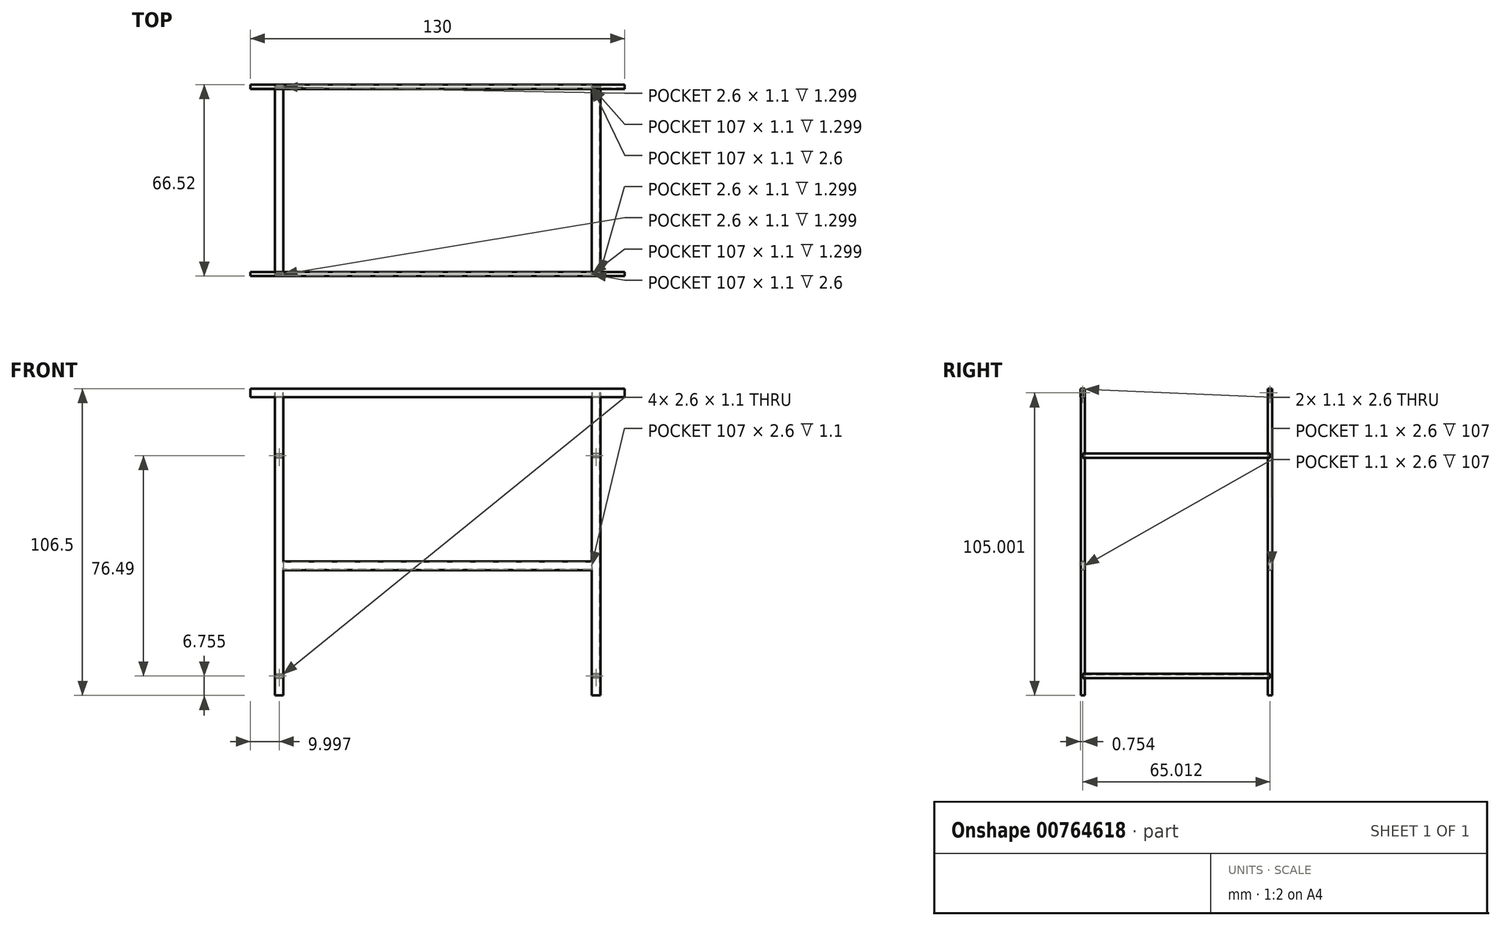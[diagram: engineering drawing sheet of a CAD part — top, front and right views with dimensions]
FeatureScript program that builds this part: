
annotation { "Feature Type Name" : "Feature", "Feature Type Description" : "" }
export const myFeature = defineFeature(function(context is Context, id is Id, definition is map)
    precondition{}
    {
        {
            var Q0;
            Q0=qCreatedBy(makeId("Top.planeOp"),FACE);
            cPlane(context, id + "F0", {"entities" : qUnion([Q0]), "cplaneType" : CPlaneType.OFFSET, "offset" : 60 * mm, "width" : 150 * mm, "height" : 150 * mm});
        }
        {
            var Q0;
            Q0=qCreatedBy(id+"F0.planeOp",FACE);
            var sketch = newSketch(context, id + "F1", { "sketchPlane" : qUnion([Q0])});
            skLineSegment(sketch, "E0", {"start": v(0, 0) * mm, "end": v(-65, 0) * mm, "construction": true});
            skLineSegment(sketch, "E1", {"start": v(-65, 0) * mm, "end": v(-65, 32.5) * mm, "construction": true});
            skSolve(sketch);
        }
        {
            var Q0;
            Q0=qCreatedBy(makeId("Right.planeOp"),FACE);
            cPlane(context, id + "F2", {"entities" : qUnion([Q0]), "cplaneType" : CPlaneType.OFFSET, "offset" : 65 * mm, "oppositeDirection" : true, "width" : 150 * mm, "height" : 150 * mm});
        }
        {
            var Q0;
            Q0=qCreatedBy(id+"F2.planeOp",FACE);
            var sketch = newSketch(context, id + "F3", { "sketchPlane" : qUnion([Q0])});
            skLineSegment(sketch, "E2.bottom", {"start": v(33.26, 61.5) * mm, "end": v(31.76, 61.5) * mm});
            skLineSegment(sketch, "E2.top", {"start": v(33.26, 58.5) * mm, "end": v(31.76, 58.5) * mm});
            skLineSegment(sketch, "E2.left", {"start": v(33.26, 61.5) * mm, "end": v(33.26, 58.5) * mm});
            skLineSegment(sketch, "E2.right", {"start": v(31.76, 61.5) * mm, "end": v(31.76, 58.5) * mm});
            skPoint(sketch, "E2.middle", {"position": v(32.5, 60) * mm});
            skLineSegment(sketch, "E3.bottom", {"start": v(33.06, 61.3) * mm, "end": v(31.96, 61.3) * mm});
            skLineSegment(sketch, "E3.top", {"start": v(33.06, 58.7) * mm, "end": v(31.96, 58.7) * mm});
            skLineSegment(sketch, "E3.left", {"start": v(33.06, 61.3) * mm, "end": v(33.06, 58.7) * mm});
            skLineSegment(sketch, "E3.right", {"start": v(31.96, 61.3) * mm, "end": v(31.96, 58.7) * mm});
            skSolve(sketch);
        }
        {
            var Q0;
            Q0=makeQuery(id+"F3.imprint","IMPRINT",FACE,{"disambiguationData":[TD([[makeQuery(id+"F3.imprint","IMPRINT",EDGE,{"derivedFrom":sQuery(id+"F3.wireOp",EDGE,"E2.bottom")}),1.0]])]});
            extrude(context, id + "F4", {"entities" : qUnion([Q0]), "depth" : 130 * mm, "offsetDistance" : 25 * mm});
        }
        {
            var Q0;
            Q0=makeQuery(id+"F4.opExtrude","SWEPT_BODY",BODY,{"disambiguationData":[OSD([sQuery(id+"F3.wireOp",EDGE,"E2.bottom"),sQuery(id+"F3.wireOp",EDGE,"E2.top"),sQuery(id+"F3.wireOp",EDGE,"E2.left"),sQuery(id+"F3.wireOp",EDGE,"E2.right"),sQuery(id+"F3.wireOp",EDGE,"E3.bottom"),sQuery(id+"F3.wireOp",EDGE,"E3.top"),sQuery(id+"F3.wireOp",EDGE,"E3.left"),sQuery(id+"F3.wireOp",EDGE,"E3.right")])]});
            var Q1;
            Q1=qCreatedBy(makeId("Front.planeOp"),FACE);
            mirror(context, id + "F5", {"entities" : qUnion([Q0]), "mirrorPlane" : qUnion([Q1])});
        }
        {
            var Q0;
            Q0=qCreatedBy(id+"F0.planeOp",FACE);
            var sketch = newSketch(context, id + "F6", { "sketchPlane" : qUnion([Q0])});
            skLineSegment(sketch, "E4", {"start": v(0, -49.29) * mm, "end": v(0, 13.23) * mm, "construction": true});
            skLineSegment(sketch, "E5", {"start": v(0, -32.5) * mm, "end": v(-55, -32.5) * mm, "construction": true});
            skLineSegment(sketch, "E6.bottom", {"start": v(-53.5, -33.25) * mm, "end": v(-56.5, -33.25) * mm});
            skLineSegment(sketch, "E6.top", {"start": v(-53.5, -31.75) * mm, "end": v(-56.5, -31.75) * mm});
            skLineSegment(sketch, "E6.left", {"start": v(-53.5, -33.25) * mm, "end": v(-53.5, -31.75) * mm});
            skLineSegment(sketch, "E6.right", {"start": v(-56.5, -33.25) * mm, "end": v(-56.5, -31.75) * mm});
            skPoint(sketch, "E6.middle", {"position": v(-55, -32.5) * mm});
            skLineSegment(sketch, "E7.bottom", {"start": v(-53.7, -33.05) * mm, "end": v(-56.3, -33.05) * mm});
            skLineSegment(sketch, "E7.top", {"start": v(-53.7, -31.95) * mm, "end": v(-56.3, -31.95) * mm});
            skLineSegment(sketch, "E7.left", {"start": v(-53.7, -33.05) * mm, "end": v(-53.7, -31.95) * mm});
            skLineSegment(sketch, "E7.right", {"start": v(-56.3, -33.05) * mm, "end": v(-56.3, -31.95) * mm});
            skSolve(sketch);
        }
        {
            var Q0;
            Q0=qSketchRegion(id+"F6",true);
            extrude(context, id + "F7", {"entities" : qUnion([Q0]), "oppositeDirection" : true, "depth" : 105 * mm, "offsetDistance" : 25 * mm});
        }
        {
            var Q0;
            Q0=makeQuery(id+"F7.opExtrude","SWEPT_BODY",BODY,{"disambiguationData":[OSD([sQuery(id+"F6.wireOp",EDGE,"E6.bottom"),sQuery(id+"F6.wireOp",EDGE,"E6.top"),sQuery(id+"F6.wireOp",EDGE,"E6.left"),sQuery(id+"F6.wireOp",EDGE,"E6.right"),sQuery(id+"F6.wireOp",EDGE,"E7.bottom"),sQuery(id+"F6.wireOp",EDGE,"E7.top"),sQuery(id+"F6.wireOp",EDGE,"E7.left"),sQuery(id+"F6.wireOp",EDGE,"E7.right")])]});
            var Q1;
            Q1=qCreatedBy(makeId("Right.planeOp"),FACE);
            mirror(context, id + "F8", {"operationType" : NewBodyOperationType.ADD, "entities" : qUnion([Q0]), "mirrorPlane" : qUnion([Q1])});
        }
        {
            var Q0;
            Q0=makeQuery(id+"F5.opPattern","COPY",BODY,{"derivedFrom":makeQuery(id+"F4.opExtrude","SWEPT_BODY",BODY,{"disambiguationData":[OSD([sQuery(id+"F3.wireOp",EDGE,"E2.bottom"),sQuery(id+"F3.wireOp",EDGE,"E2.top"),sQuery(id+"F3.wireOp",EDGE,"E2.left"),sQuery(id+"F3.wireOp",EDGE,"E2.right"),sQuery(id+"F3.wireOp",EDGE,"E3.bottom"),sQuery(id+"F3.wireOp",EDGE,"E3.top"),sQuery(id+"F3.wireOp",EDGE,"E3.left"),sQuery(id+"F3.wireOp",EDGE,"E3.right")])]}),"instanceName":"1"});
            var Q1;
            Q1=qCreatedBy(makeId("Front.planeOp"),FACE);
            mirror(context, id + "F9", {"operationType" : NewBodyOperationType.ADD, "entities" : qUnion([Q0]), "mirrorPlane" : qUnion([Q1])});
        }
        {
            var Q0;
            Q0=qCreatedBy(makeId("Front.planeOp"),FACE);
            var sketch = newSketch(context, id + "F10", { "sketchPlane" : qUnion([Q0])});
            skLineSegment(sketch, "E8", {"start": v(53.5, 56.46) * mm, "end": v(56.5, 56.46) * mm, "construction": true});
            skLineSegment(sketch, "E9", {"start": v(55, 58.24) * mm, "end": v(55, 38.24) * mm, "construction": true});
            skPoint(sketch, "E9.startSnap0", {"position": v(55, 56.46) * mm});
            skLineSegment(sketch, "E10.bottom", {"start": v(56.5, 39) * mm, "end": v(53.5, 39) * mm});
            skLineSegment(sketch, "E10.top", {"start": v(56.5, 37.5) * mm, "end": v(53.5, 37.5) * mm});
            skLineSegment(sketch, "E10.left", {"start": v(56.5, 39) * mm, "end": v(56.5, 37.5) * mm});
            skLineSegment(sketch, "E10.right", {"start": v(53.5, 39) * mm, "end": v(53.5, 37.5) * mm});
            skPoint(sketch, "E10.middle", {"position": v(55, 38.24) * mm});
            skLineSegment(sketch, "E11.bottom", {"start": v(56.3, 38.8) * mm, "end": v(53.7, 38.8) * mm});
            skLineSegment(sketch, "E11.top", {"start": v(56.3, 37.7) * mm, "end": v(53.7, 37.7) * mm});
            skLineSegment(sketch, "E11.left", {"start": v(56.3, 38.8) * mm, "end": v(56.3, 37.7) * mm});
            skLineSegment(sketch, "E11.right", {"start": v(53.7, 38.8) * mm, "end": v(53.7, 37.7) * mm});
            skSolve(sketch);
        }
        {
            var Q0;
            Q0=qSketchRegion(id+"F10",true);
            extrude(context, id + "F11", {"entities" : qUnion([Q0]), "endBound" : BoundingType.SYMMETRIC, "depth" : 65 * mm, "offsetDistance" : 25 * mm});
        }
        {
            var Q0;
            Q0=makeQuery(id+"F11.opExtrude","SWEPT_BODY",BODY,{"disambiguationData":[OSD([sQuery(id+"F10.wireOp",EDGE,"E10.bottom"),sQuery(id+"F10.wireOp",EDGE,"E10.top"),sQuery(id+"F10.wireOp",EDGE,"E10.left"),sQuery(id+"F10.wireOp",EDGE,"E10.right"),sQuery(id+"F10.wireOp",EDGE,"E11.bottom"),sQuery(id+"F10.wireOp",EDGE,"E11.top"),sQuery(id+"F10.wireOp",EDGE,"E11.left"),sQuery(id+"F10.wireOp",EDGE,"E11.right")])]});
            var Q1;
            Q1=qCreatedBy(makeId("Top.planeOp"),FACE);
            mirror(context, id + "F12", {"entities" : qUnion([Q0]), "mirrorPlane" : qUnion([Q1])});
        }
        {
            var Q0;
            Q0=makeQuery(id+"F11.opExtrude","SWEPT_BODY",BODY,{"disambiguationData":[OSD([sQuery(id+"F10.wireOp",EDGE,"E10.bottom"),sQuery(id+"F10.wireOp",EDGE,"E10.top"),sQuery(id+"F10.wireOp",EDGE,"E10.left"),sQuery(id+"F10.wireOp",EDGE,"E10.right"),sQuery(id+"F10.wireOp",EDGE,"E11.bottom"),sQuery(id+"F10.wireOp",EDGE,"E11.top"),sQuery(id+"F10.wireOp",EDGE,"E11.left"),sQuery(id+"F10.wireOp",EDGE,"E11.right")])]});
            var Q1;
            Q1=qCreatedBy(makeId("Right.planeOp"),FACE);
            mirror(context, id + "F13", {"entities" : qUnion([Q0]), "mirrorPlane" : qUnion([Q1])});
        }
        {
            var Q0;
            Q0=makeQuery(id+"F13.opPattern","COPY",BODY,{"derivedFrom":makeQuery(id+"F11.opExtrude","SWEPT_BODY",BODY,{"disambiguationData":[OSD([sQuery(id+"F10.wireOp",EDGE,"E10.bottom"),sQuery(id+"F10.wireOp",EDGE,"E10.top"),sQuery(id+"F10.wireOp",EDGE,"E10.left"),sQuery(id+"F10.wireOp",EDGE,"E10.right"),sQuery(id+"F10.wireOp",EDGE,"E11.bottom"),sQuery(id+"F10.wireOp",EDGE,"E11.top"),sQuery(id+"F10.wireOp",EDGE,"E11.left"),sQuery(id+"F10.wireOp",EDGE,"E11.right")])]}),"instanceName":"1"});
            var Q1;
            Q1=qCreatedBy(makeId("Top.planeOp"),FACE);
            mirror(context, id + "F14", {"entities" : qUnion([Q0]), "mirrorPlane" : qUnion([Q1])});
        }
        {
            var Q0;
            Q0=qCreatedBy(makeId("Right.planeOp"),FACE);
            var sketch = newSketch(context, id + "F15", { "sketchPlane" : qUnion([Q0])});
            skLineSegment(sketch, "E12", {"start": v(-33.25, 0) * mm, "end": v(-31.76, 0) * mm, "construction": true});
            skLineSegment(sketch, "E13.bottom", {"start": v(-31.76, 1.5) * mm, "end": v(-33.26, 1.5) * mm});
            skLineSegment(sketch, "E13.top", {"start": v(-31.76, -1.5) * mm, "end": v(-33.26, -1.5) * mm});
            skLineSegment(sketch, "E13.left", {"start": v(-31.76, 1.5) * mm, "end": v(-31.76, -1.5) * mm});
            skLineSegment(sketch, "E13.right", {"start": v(-33.26, 1.5) * mm, "end": v(-33.26, -1.5) * mm});
            skPoint(sketch, "E13.middle", {"position": v(-32.5, 0) * mm});
            skLineSegment(sketch, "E14.bottom", {"start": v(-31.96, 1.3) * mm, "end": v(-33.06, 1.3) * mm});
            skLineSegment(sketch, "E14.top", {"start": v(-31.96, -1.3) * mm, "end": v(-33.06, -1.3) * mm});
            skLineSegment(sketch, "E14.left", {"start": v(-31.96, 1.3) * mm, "end": v(-31.96, -1.3) * mm});
            skLineSegment(sketch, "E14.right", {"start": v(-33.06, 1.3) * mm, "end": v(-33.06, -1.3) * mm});
            skSolve(sketch);
        }
        {
            var Q0;
            Q0 = qSketchRegion(id + "F15", true);
            extrude(context, id + "F16", {"entities" : qUnion([Q0]), "endBound" : BoundingType.SYMMETRIC, "depth" : 107 * mm, "offsetDistance" : 25 * mm});
        }
        {
            var Q0;
            Q0=makeQuery(id+"F16.opExtrude","SWEPT_BODY",BODY,{"disambiguationData":[OSD([sQuery(id+"F15.wireOp",EDGE,"E13.bottom"),sQuery(id+"F15.wireOp",EDGE,"E13.top"),sQuery(id+"F15.wireOp",EDGE,"E13.left"),sQuery(id+"F15.wireOp",EDGE,"E13.right"),sQuery(id+"F15.wireOp",EDGE,"E14.bottom"),sQuery(id+"F15.wireOp",EDGE,"E14.top"),sQuery(id+"F15.wireOp",EDGE,"E14.left"),sQuery(id+"F15.wireOp",EDGE,"E14.right")])]});
            var Q1;
            Q1=qCreatedBy(makeId("Front.planeOp"),FACE);
            mirror(context, id + "F17", {"operationType" : NewBodyOperationType.ADD, "entities" : qUnion([Q0]), "mirrorPlane" : qUnion([Q1])});
        }
    });
